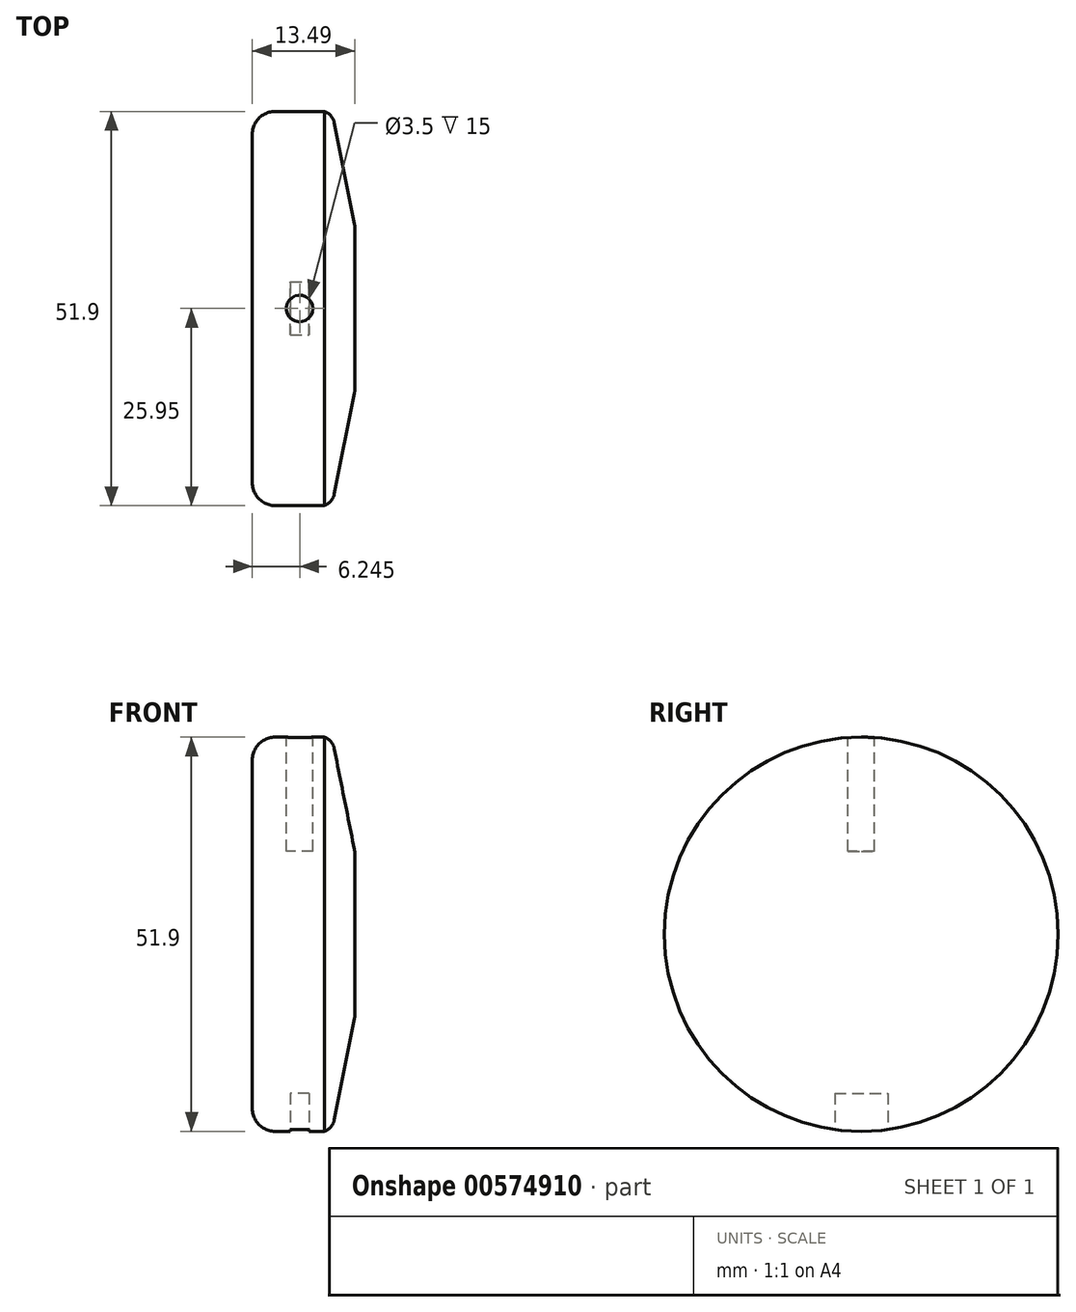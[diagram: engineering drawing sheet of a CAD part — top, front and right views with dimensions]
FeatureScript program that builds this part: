
annotation { "Feature Type Name" : "Feature", "Feature Type Description" : "" }
export const myFeature = defineFeature(function(context is Context, id is Id, definition is map)
    precondition{}
    {
        {
            var Q0;
            Q0=qCreatedBy(makeId("Right.planeOp"),FACE);
            var sketch = newSketch(context, id + "F0", { "sketchPlane" : qUnion([Q0])});
            skCircle(sketch, "E0", {"center": v(0, 0) * mm, "radius": 25.95 * mm});
            skSolve(sketch);
        }
        {
            var Q0;
            Q0=makeQuery(id+"F0.imprint","IMPRINT",FACE,{"disambiguationData":[TD([[makeQuery(id+"F0.imprint","IMPRINT",EDGE,{"derivedFrom":sQuery(id+"F0.wireOp",EDGE,"E0")}),1.0]])]});
            extrude(context, id + "F1", {"entities" : qUnion([Q0]), "depth" : 4 * mm, "offsetDistance" : 25 * mm});
        }
        {
            var Q0;
            Q0=makeQuery(id+"F1.opExtrude","CAP_EDGE",EDGE,{"disambiguationData":[OSD([sQuery(id+"F0.wireOp",EDGE,"E0")])],"isStart":false});
            chamfer(context, id + "F2", {"entities" : qUnion([Q0]), "chamferType" : ChamferType.TWO_OFFSETS, "width1" : 15 * mm, "oppositeDirection" : false, "width2" : 3 * mm, "tangentPropagation" : true});
        }
        {
            var Q0;
            Q0=makeQuery(id+"F1.opExtrude","CAP_FACE",FACE,{"disambiguationData":[OSD([sQuery(id+"F0.wireOp",EDGE,"E0")])],"isStart":true});
            extrude(context, id + "F3", {"entities" : qUnion([Q0]), "depth" : (13.5 - 4) * mm, "offsetDistance" : 25 * mm});
        }
        {
            var Q0;
            Q0=makeQuery(id+"F3.opExtrude","CAP_EDGE",EDGE,{"disambiguationData":[OSD([sQuery(id+"F0.wireOp",EDGE,"E0")])],"isStart":false});
            fillet(context, id + "F4", {"entities" : qUnion([Q0]), "radius" : 3 * mm, "tangentPropagation" : true, "allowEdgeOverflow" : false});
        }
        {
            var Q0;
            {var subQ0=sQuery(id+"F0.wireOp",EDGE,"E0");Q0=makeQuery(id+"F2.opChamfer","BLEND_EDGE",EDGE,{"blendedFrom":[makeQuery(id+"F1.opExtrude","CAP_EDGE",EDGE,{"disambiguationData":[OSD([subQ0])],"isStart":false}),makeQuery(id+"F1.opExtrude","SWEPT_FACE",FACE,{"disambiguationData":[OSD([subQ0])]})],"blendedInto":[makeQuery(id+"F1.opExtrude","SWEPT_FACE",FACE,{"disambiguationData":[OSD([subQ0])]})]});}
            var Q1;
            {var subQ0=sQuery(id+"F0.wireOp",EDGE,"E0");Q1=makeQuery(id+"F2.opChamfer","BLEND_EDGE",EDGE,{"blendedFrom":[makeQuery(id+"F1.opExtrude","CAP_EDGE",EDGE,{"disambiguationData":[OSD([subQ0])],"isStart":false}),makeQuery(id+"F1.opExtrude","CAP_FACE",FACE,{"disambiguationData":[OSD([subQ0])],"isStart":false})],"blendedInto":[makeQuery(id+"F1.opExtrude","CAP_FACE",FACE,{"disambiguationData":[OSD([subQ0])],"isStart":false})]});}
            fillet(context, id + "F5", {"entities" : qUnion([Q0, Q1]), "radius" : 2 * mm, "tangentPropagation" : true, "allowEdgeOverflow" : false});
        }
        {
            var Q0;
            Q0=qCreatedBy(makeId("Top.planeOp"),FACE);
            cPlane(context, id + "F6", {"entities" : qUnion([Q0]), "cplaneType" : CPlaneType.OFFSET, "offset" : (51.9 / 2) * mm, "width" : 150 * mm, "height" : 150 * mm});
        }
        {
            var Q0;
            Q0=qCreatedBy(id+"F6.planeOp",FACE);
            var sketch = newSketch(context, id + "F7", { "sketchPlane" : qUnion([Q0])});
            skPoint(sketch, "E1", {"position": v(-3.25, 0) * mm});
            skCircle(sketch, "E2", {"center": v(-3.25, 0) * mm, "radius": 1.75 * mm});
            skLineSegment(sketch, "E3.0", {"start": v(-6.5, 25.95) * mm, "end": v(-6.5, -25.95) * mm, "construction": true});
            skLineSegment(sketch, "E4.0", {"start": v(0, 25.95) * mm, "end": v(0, -25.95) * mm, "construction": true});
            skLineSegment(sketch, "E5", {"start": v(-6.5, 0) * mm, "end": v(-3.25, 0) * mm, "construction": true});
            skLineSegment(sketch, "E6", {"start": v(0, 0) * mm, "end": v(-3.25, 0) * mm, "construction": true});
            skSolve(sketch);
        }
        {
            var Q0;
            Q0=makeQuery(id+"F7.imprint","IMPRINT",FACE,{"disambiguationData":[TD([[makeQuery(id+"F7.imprint","IMPRINT",EDGE,{"derivedFrom":sQuery(id+"F7.wireOp",EDGE,"E2")}),1.0]])]});
            extrude(context, id + "F8", {"entities" : qUnion([Q0]), "operationType" : NewBodyOperationType.REMOVE, "oppositeDirection" : true, "depth" : 15 * mm, "offsetDistance" : 25 * mm});
        }
        {
            var Q0;
            Q0=qCreatedBy(makeId("Top.planeOp"),FACE);
            cPlane(context, id + "F9", {"entities" : qUnion([Q0]), "cplaneType" : CPlaneType.OFFSET, "offset" : (51.9 / 2) * mm, "oppositeDirection" : true, "width" : 150 * mm, "height" : 150 * mm});
        }
        {
            var Q0;
            Q0=qCreatedBy(id+"F9.planeOp",FACE);
            var sketch = newSketch(context, id + "F10", { "sketchPlane" : qUnion([Q0])});
            skLineSegment(sketch, "E7.bottom", {"start": v(-2, -3.5) * mm, "end": v(-4.5, -3.5) * mm});
            skLineSegment(sketch, "E7.top", {"start": v(-2, 3.5) * mm, "end": v(-4.5, 3.5) * mm});
            skLineSegment(sketch, "E7.left", {"start": v(-2, -3.5) * mm, "end": v(-2, 3.5) * mm});
            skLineSegment(sketch, "E7.right", {"start": v(-4.5, -3.5) * mm, "end": v(-4.5, 3.5) * mm});
            skPoint(sketch, "E7.middle", {"position": v(-3.25, 0) * mm});
            skLineSegment(sketch, "E8", {"start": v(-3.25, 0) * mm, "end": v(0, 0) * mm, "construction": true});
            skLineSegment(sketch, "E9.0", {"start": v(-6.5, 25.95) * mm, "end": v(-6.5, -25.95) * mm, "construction": true});
            skLineSegment(sketch, "E10", {"start": v(-3.25, 0) * mm, "end": v(-6.5, 0) * mm, "construction": true});
            skSolve(sketch);
        }
        {
            var Q0;
            Q0=makeQuery(id+"F10.imprint","IMPRINT",FACE,{"disambiguationData":[TD([[makeQuery(id+"F10.imprint","IMPRINT",EDGE,{"derivedFrom":sQuery(id+"F10.wireOp",EDGE,"E7.bottom")}),-1.0]])]});
            extrude(context, id + "F11", {"entities" : qUnion([Q0]), "operationType" : NewBodyOperationType.REMOVE, "depth" : 5 * mm, "offsetDistance" : 25 * mm});
        }
    });
